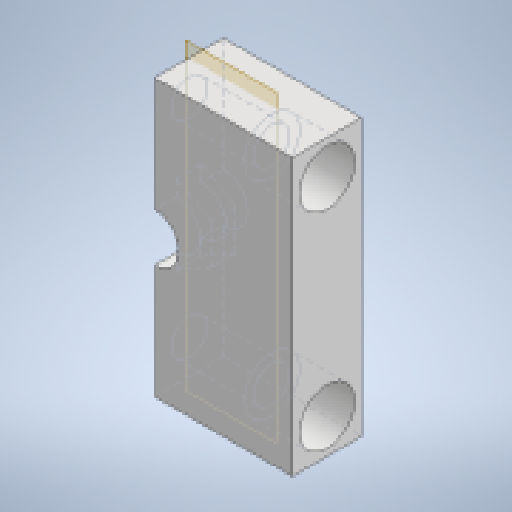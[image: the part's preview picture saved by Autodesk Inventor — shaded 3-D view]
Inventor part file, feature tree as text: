
AUTODESK INVENTOR PART (.ipt)
format: ipt  version: 2023 (Build 270158000, 158)  size: 194,560 bytes
history: native  units: mm
features: sketch x7, extrude x6, plane x1
ambient origin geometry x8: Origin, YZ Plane, XZ Plane, XY Plane, X Axis, Y Axis, Z Axis, Center Point
bodies: Solid1 (feature_tree)
feature tree (14):
  extrude  "Extrusion1"  Depth=20.0mm
  plane  "Work Plane1"
  extrude  "Extrusion2"  Depth=5.0mm
  extrude  "Extrusion3"  Depth=1.8mm
  extrude  "Extrusion4"  Depth=2.5mm
  extrude  "Extrusion5"  Depth=2.5mm
  sketch  "Sketch6"  dims[d21=2.5mm d22=2.6mm]
  extrude  "Extrusion6"  Depth=2.5mm
  sketch  "Sketch1"  dims[d0=20.0mm d1=20.0mm]
  sketch  "Sketch2"  dims[d10=5.0mm d11=0.0mm d12=5.0mm]
  sketch  "Sketch3"  dims[d13=1.8mm d14=0.0mm d15=3.5mm]
  sketch  "Sketch4"  dims[d16=8.0mm d17=0.0mm d18=2.5mm]
  sketch  "Sketch5"  dims[d19=2.5mm d20=2.5mm]
  sketch  "Sketch7"  dims[d23=2.6mm d24=25.0mm d25=0.0mm d26=4.0mm d27=4.0mm d28=4.0mm d29=0.0mm d30=5.0mm d31=5.0mm d32=5.0mm d33=5.0mm d34=10.0mm d35=0.0mm]
